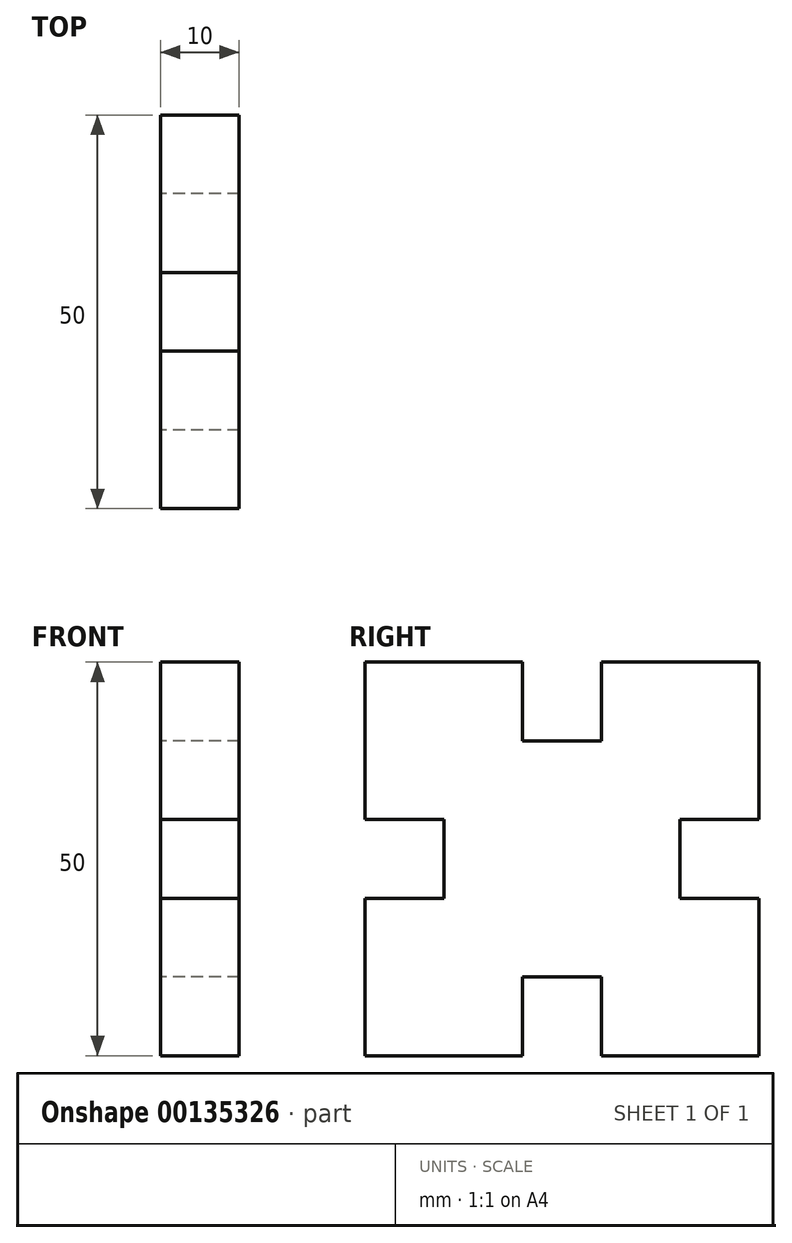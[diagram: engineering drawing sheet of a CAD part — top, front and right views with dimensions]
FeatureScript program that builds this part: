
annotation { "Feature Type Name" : "Feature", "Feature Type Description" : "" }
export const myFeature = defineFeature(function(context is Context, id is Id, definition is map)
    precondition{}
    {
        {
            var Q0;
            Q0=qCreatedBy(makeId("Right.planeOp"),FACE);
            var sketch = newSketch(context, id + "F0", { "sketchPlane" : qUnion([Q0])});
            skLineSegment(sketch, "E0.bottom", {"start": v(-50, 50) * mm, "end": v(0, 50) * mm});
            skLineSegment(sketch, "E0.top", {"start": v(-50, 0) * mm, "end": v(0, 0) * mm});
            skLineSegment(sketch, "E0.left", {"start": v(-50, 50) * mm, "end": v(-50, 0) * mm});
            skLineSegment(sketch, "E0.right", {"start": v(0, 50) * mm, "end": v(0, 0) * mm});
            skLineSegment(sketch, "E1.bottom", {"start": v(-30, 50) * mm, "end": v(-20, 50) * mm});
            skLineSegment(sketch, "E1.top", {"start": v(-30, 40) * mm, "end": v(-20, 40) * mm});
            skLineSegment(sketch, "E1.left", {"start": v(-30, 50) * mm, "end": v(-30, 40) * mm});
            skLineSegment(sketch, "E1.right", {"start": v(-20, 50) * mm, "end": v(-20, 40) * mm});
            skLineSegment(sketch, "E2.bottom", {"start": v(0, 30) * mm, "end": v(-10, 30) * mm});
            skLineSegment(sketch, "E2.top", {"start": v(0, 20) * mm, "end": v(-10, 20) * mm});
            skLineSegment(sketch, "E2.left", {"start": v(0, 30) * mm, "end": v(0, 20) * mm});
            skLineSegment(sketch, "E2.right", {"start": v(-10, 30) * mm, "end": v(-10, 20) * mm});
            skLineSegment(sketch, "E3.bottom", {"start": v(-30, 0) * mm, "end": v(-20, 0) * mm});
            skLineSegment(sketch, "E3.top", {"start": v(-30, 10) * mm, "end": v(-20, 10) * mm});
            skLineSegment(sketch, "E3.left", {"start": v(-30, 0) * mm, "end": v(-30, 10) * mm});
            skLineSegment(sketch, "E3.right", {"start": v(-20, 0) * mm, "end": v(-20, 10) * mm});
            skLineSegment(sketch, "E4.bottom", {"start": v(-50, 30) * mm, "end": v(-40, 30) * mm});
            skLineSegment(sketch, "E4.top", {"start": v(-50, 20) * mm, "end": v(-40, 20) * mm});
            skLineSegment(sketch, "E4.left", {"start": v(-50, 30) * mm, "end": v(-50, 20) * mm});
            skLineSegment(sketch, "E4.right", {"start": v(-40, 30) * mm, "end": v(-40, 20) * mm});
            skSolve(sketch);
        }
        {
            var Q0;
            Q0=makeQuery(id+"F0.imprint","IMPRINT",FACE,{"disambiguationData":[TD([[makeQuery(id+"F0.imprint","IMPRINT",EDGE,{"derivedFrom":sQuery(id+"F0.wireOp",EDGE,"E1.top")}),-1.0]])]});
            extrude(context, id + "F1", {"entities" : qUnion([Q0]), "depth" : 10 * mm});
        }
    });
